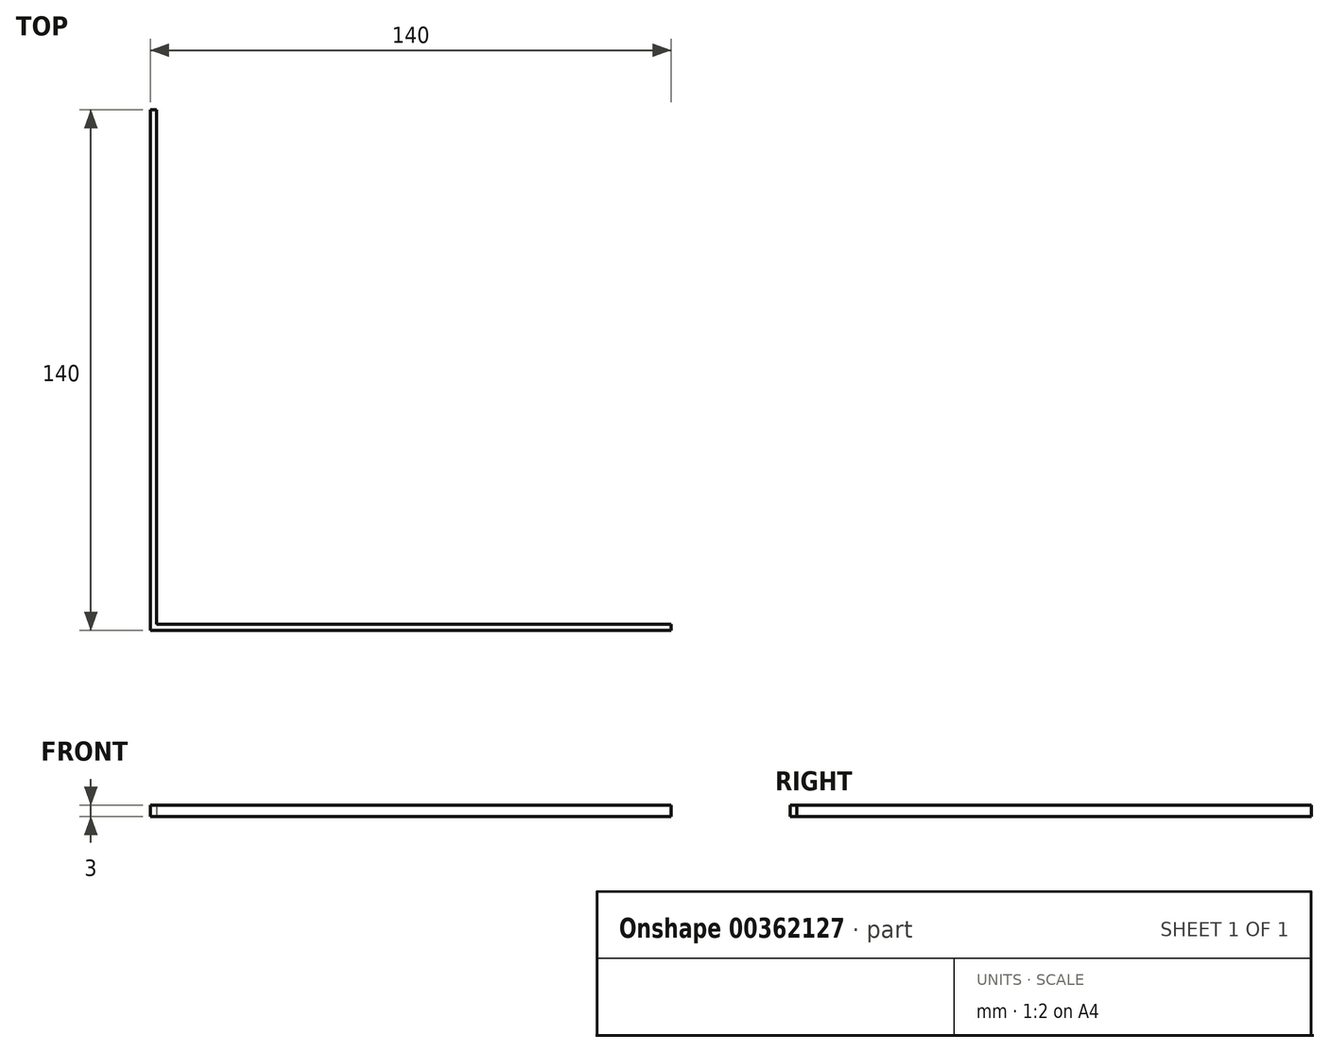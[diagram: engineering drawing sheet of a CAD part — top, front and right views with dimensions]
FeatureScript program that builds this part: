
annotation { "Feature Type Name" : "Feature", "Feature Type Description" : "" }
export const myFeature = defineFeature(function(context is Context, id is Id, definition is map)
    precondition{}
    {
        {
            var Q0;
            Q0=qCreatedBy(makeId("Top.planeOp"),FACE);
            var sketch = newSketch(context, id + "F0", { "sketchPlane" : qUnion([Q0])});
            skLineSegment(sketch, "E0.bottom", {"start": v(0, 0) * mm, "end": v(140, 0) * mm});
            skLineSegment(sketch, "E0.top", {"start": v(0, 140) * mm, "end": v(140, 140) * mm});
            skLineSegment(sketch, "E0.left", {"start": v(0, 0) * mm, "end": v(0, 140) * mm});
            skLineSegment(sketch, "E0.right", {"start": v(140, 0) * mm, "end": v(140, 140) * mm});
            skLineSegment(sketch, "E1.bottom", {"start": v(140, 140) * mm, "end": v(1.7, 140) * mm});
            skLineSegment(sketch, "E1.top", {"start": v(140, 1.7) * mm, "end": v(1.7, 1.7) * mm});
            skLineSegment(sketch, "E1.left", {"start": v(140, 140) * mm, "end": v(140, 1.7) * mm});
            skLineSegment(sketch, "E1.right", {"start": v(1.7, 140) * mm, "end": v(1.7, 1.7) * mm});
            skSolve(sketch);
        }
        {
            var Q0;
            Q0=makeQuery(id+"F0.imprint","IMPRINT",FACE,{"disambiguationData":[TD([[makeQuery(id+"F0.imprint","IMPRINT",EDGE,{"derivedFrom":sQuery(id+"F0.wireOp",EDGE,"E0.bottom")}),1.0]])]});
            extrude(context, id + "F1", {"entities" : qUnion([Q0]), "depth" : 3 * mm, "offsetDistance" : 25 * mm});
        }
    });
